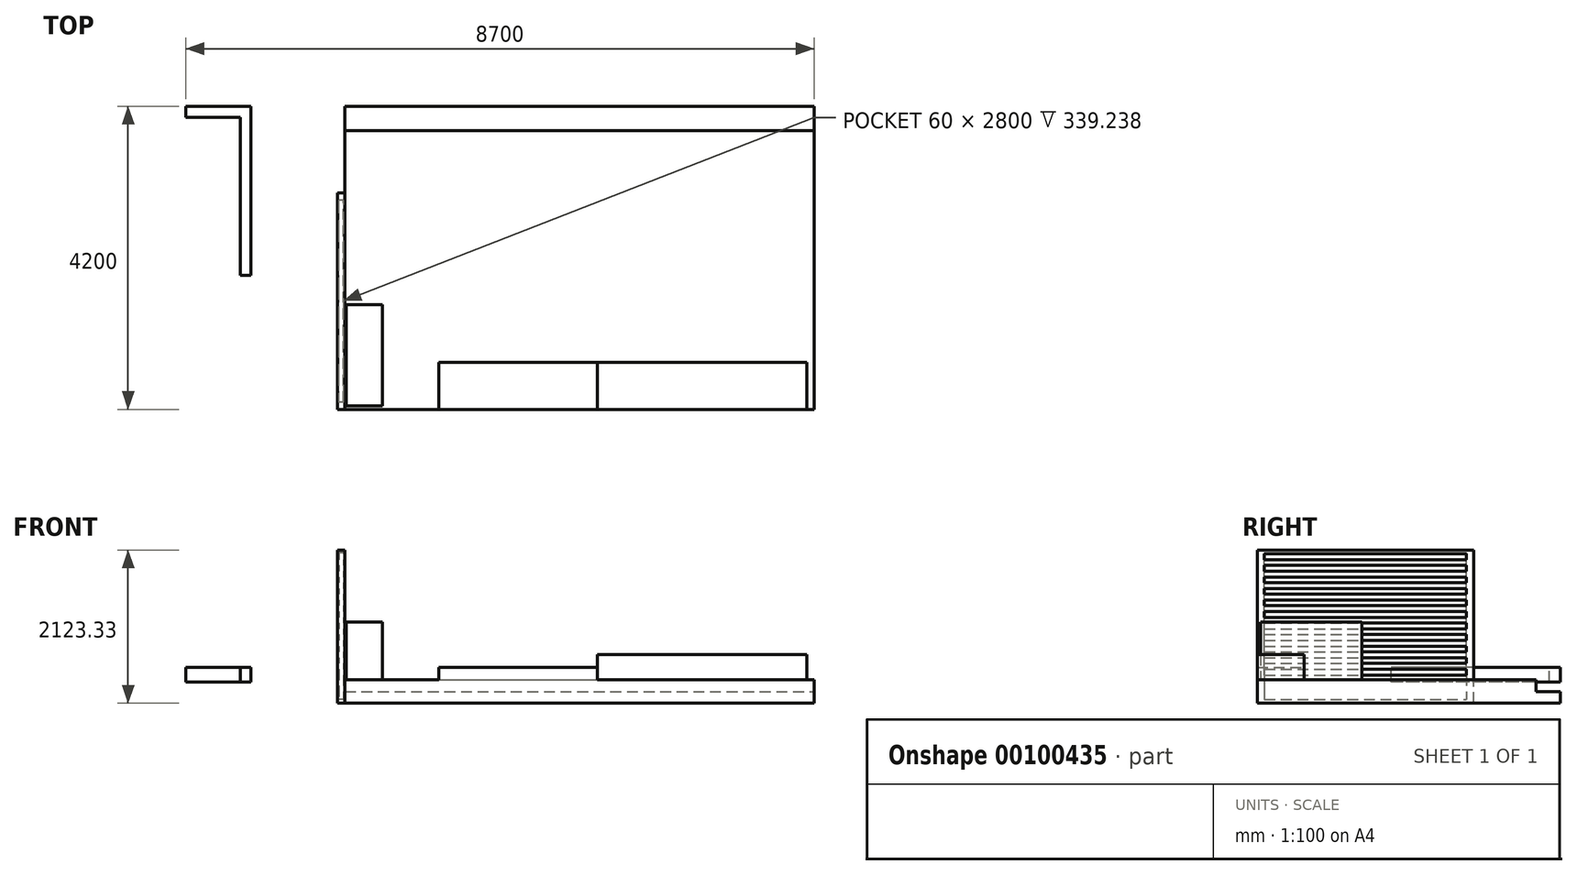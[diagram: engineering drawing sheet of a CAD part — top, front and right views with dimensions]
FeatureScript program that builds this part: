
annotation { "Feature Type Name" : "Feature", "Feature Type Description" : "" }
export const myFeature = defineFeature(function(context is Context, id is Id, definition is map)
    precondition{}
    {
        {
            var Q0;
            Q0=qCreatedBy(makeId("Top.planeOp"),FACE);
            var sketch = newSketch(context, id + "F0", { "sketchPlane" : qUnion([Q0])});
            skLineSegment(sketch, "E0.bottom", {"start": v(0, 0) * mm, "end": v(6600, 0) * mm});
            skLineSegment(sketch, "E0.top", {"start": v(0, -11600) * mm, "end": v(6600, -11600) * mm});
            skLineSegment(sketch, "E0.left", {"start": v(0, 0) * mm, "end": v(0, -11600) * mm});
            skLineSegment(sketch, "E0.right", {"start": v(6600, 0) * mm, "end": v(6600, -11600) * mm});
            skLineSegment(sketch, "E1.bottom", {"start": v(-1200, 1860) * mm, "end": v(0, 1860) * mm});
            skLineSegment(sketch, "E1.top", {"start": v(-1200, -4000) * mm, "end": v(0, -4000) * mm});
            skLineSegment(sketch, "E1.left", {"start": v(-1200, 1860) * mm, "end": v(-1200, -4000) * mm});
            skLineSegment(sketch, "E1.right", {"start": v(0, 1860) * mm, "end": v(0, -4000) * mm});
            skLineSegment(sketch, "E2", {"start": v(-2100, 10600) * mm, "end": v(-2100, 4000) * mm});
            skLineSegment(sketch, "E3", {"start": v(-2100, 4000) * mm, "end": v(-7856.97, 4000) * mm});
            skLineSegment(sketch, "E4", {"start": v(-2100, 10600) * mm, "end": v(-7856.97, 10600) * mm});
            skLineSegment(sketch, "E5", {"start": v(-2100, 4200) * mm, "end": v(-1200, 4200) * mm});
            skLineSegment(sketch, "E6", {"start": v(-1200, 4200) * mm, "end": v(-1200, 1860) * mm});
            skLineSegment(sketch, "E7", {"start": v(300, 0) * mm, "end": v(300, 1860) * mm});
            skLineSegment(sketch, "E8", {"start": v(300, 1860) * mm, "end": v(0, 1860) * mm});
            skLineSegment(sketch, "E9", {"start": v(230, 1860) * mm, "end": v(230, 0) * mm});
            skLineSegment(sketch, "E10.0", {"start": v(-1350, 4050) * mm, "end": v(-1350, 1860) * mm});
            skLineSegment(sketch, "E10.1", {"start": v(-2100, 4050) * mm, "end": v(-1350, 4050) * mm});
            skSolve(sketch);
        }
        {
            var Q0;
            Q0=qCreatedBy(makeId("Top.planeOp"),FACE);
            var sketch = newSketch(context, id + "F1", { "sketchPlane" : qUnion([Q0])});
            skLineSegment(sketch, "E11.0", {"start": v(-2100, 4200) * mm, "end": v(-1200, 4200) * mm});
            skLineSegment(sketch, "E11.1", {"start": v(-2100, 4050) * mm, "end": v(-1350, 4050) * mm});
            skLineSegment(sketch, "E11.2", {"start": v(-1350, 4050) * mm, "end": v(-1350, 1860) * mm});
            skLineSegment(sketch, "E11.3", {"start": v(-1200, 4200) * mm, "end": v(-1200, 1860) * mm});
            skLineSegment(sketch, "E12", {"start": v(-2100, 4200) * mm, "end": v(-2100, 4050) * mm});
            skLineSegment(sketch, "E13", {"start": v(-1200, 1860) * mm, "end": v(-1350, 1860) * mm});
            skSolve(sketch);
        }
        {
            var Q0;
            Q0 = qSketchRegion(id + "F1", true);
            extrude(context, id + "F2", {"entities" : qUnion([Q0]), "oppositeDirection" : true, "depth" : 200 * mm, "offsetDistance" : 25 * mm});
        }
        {
            var Q0;
            Q0=qCreatedBy(makeId("Top.planeOp"),FACE);
            var sketch = newSketch(context, id + "F3", { "sketchPlane" : qUnion([Q0])});
            skLineSegment(sketch, "E14", {"start": v(-1200, 4200) * mm, "end": v(100, 4200) * mm, "construction": true});
            skLineSegment(sketch, "E15", {"start": v(6600, 4200) * mm, "end": v(6600, 0) * mm});
            skLineSegment(sketch, "E16", {"start": v(100, 4200) * mm, "end": v(100, 0) * mm});
            skLineSegment(sketch, "E17", {"start": v(100, 4200) * mm, "end": v(6600, 4200) * mm});
            skLineSegment(sketch, "E18.1", {"start": v(300, 0) * mm, "end": v(6600, 0) * mm});
            skPoint(sketch, "E19.orphan", {"position": v(0, 0) * mm});
            skLineSegment(sketch, "E20", {"start": v(300, 0) * mm, "end": v(100, 0) * mm});
            skSolve(sketch);
        }
        {
            var Q0;
            Q0=qCreatedBy(makeId("Top.planeOp"),FACE);
            var sketch = newSketch(context, id + "F4", { "sketchPlane" : qUnion([Q0])});
            skLineSegment(sketch, "E21.bottom", {"start": v(1450, 0) * mm, "end": v(3550, 0) * mm});
            skLineSegment(sketch, "E21.top", {"start": v(1450, -350) * mm, "end": v(3550, -350) * mm});
            skLineSegment(sketch, "E21.left", {"start": v(1450, 0) * mm, "end": v(1450, -350) * mm});
            skLineSegment(sketch, "E21.right", {"start": v(3550, 0) * mm, "end": v(3550, -350) * mm});
            skLineSegment(sketch, "E22", {"start": v(2350, 0) * mm, "end": v(2350, -350) * mm});
            skLineSegment(sketch, "E23", {"start": v(2350, -175) * mm, "end": v(3550, -175) * mm});
            skSolve(sketch);
        }
        {
            var Q0;
            Q0=qCreatedBy(makeId("Top.planeOp"),FACE);
            cPlane(context, id + "F5", {"entities" : qUnion([Q0]), "cplaneType" : CPlaneType.OFFSET, "offset" : (500 / 3) * mm, "oppositeDirection" : true, "width" : 150 * mm, "height" : 150 * mm});
        }
        {
            var Q0;
            Q0=qCreatedBy(makeId("Top.planeOp"),FACE);
            cPlane(context, id + "F6", {"entities" : qUnion([Q0]), "cplaneType" : CPlaneType.OFFSET, "offset" : (500 / 3 * 2) * mm, "oppositeDirection" : true, "width" : 150 * mm, "height" : 150 * mm});
        }
        {
            var Q0;
            Q0=qCreatedBy(id+"F6.planeOp",FACE);
            cPlane(context, id + "F7", {"entities" : qUnion([Q0]), "cplaneType" : CPlaneType.OFFSET, "offset" : 160 * mm, "oppositeDirection" : true, "width" : 150 * mm, "height" : 150 * mm});
        }
        {
            var Q0;
            Q0=qCreatedBy(makeId("Top.planeOp"),FACE);
            var sketch = newSketch(context, id + "F8", { "sketchPlane" : qUnion([Q0])});
            skLineSegment(sketch, "E24.bottom", {"start": v(1400, 0) * mm, "end": v(3600, 0) * mm});
            skLineSegment(sketch, "E24.top", {"start": v(1400, 650) * mm, "end": v(3600, 650) * mm});
            skLineSegment(sketch, "E24.left", {"start": v(1400, 0) * mm, "end": v(1400, 650) * mm});
            skLineSegment(sketch, "E24.right", {"start": v(3600, 0) * mm, "end": v(3600, 650) * mm});
            skSolve(sketch);
        }
        {
            var Q0;
            Q0 = qSketchRegion(id + "F8", true);
            var Q1;
            Q1=qCreatedBy(id+"F7.planeOp",FACE);
            extrude(context, id + "F9", {"entities" : qUnion([Q0]), "endBound" : BoundingType.UP_TO_SURFACE, "oppositeDirection" : true, "depth" : 25 * mm, "endBoundEntityFace" : qUnion([Q1]), "offsetDistance" : 25 * mm});
        }
        {
            var Q0;
            Q0=qCreatedBy(id+"F5.planeOp",FACE);
            var sketch = newSketch(context, id + "F10", { "sketchPlane" : qUnion([Q0])});
            skLineSegment(sketch, "E25", {"start": v(111.53, 3862.22) * mm, "end": v(6600, 3862.22) * mm});
            skSolve(sketch);
        }
        {
            var Q0;
            Q0=qCreatedBy(id+"F5.planeOp",FACE);
            var sketch = newSketch(context, id + "F11", { "sketchPlane" : qUnion([Q0])});
            skLineSegment(sketch, "E26.0", {"start": v(100, 3862.22) * mm, "end": v(6600, 3862.22) * mm});
            skLineSegment(sketch, "E26.1", {"start": v(6600, 3862.22) * mm, "end": v(6600, 0) * mm});
            skPoint(sketch, "E27.orphan", {"position": v(6600, 4200) * mm});
            skLineSegment(sketch, "E28", {"start": v(100, 3862.22) * mm, "end": v(100, 0) * mm});
            skPoint(sketch, "E29.orphan", {"position": v(111.53, 3862.22) * mm});
            skLineSegment(sketch, "E30", {"start": v(100, 0) * mm, "end": v(1400, 0) * mm});
            skLineSegment(sketch, "E31.0", {"start": v(1400, 0) * mm, "end": v(1400, 650) * mm});
            skLineSegment(sketch, "E31.1", {"start": v(1400, 650) * mm, "end": v(3600, 650) * mm});
            skLineSegment(sketch, "E31.2", {"start": v(3600, 0) * mm, "end": v(3600, 650) * mm});
            skLineSegment(sketch, "E32", {"start": v(3600, 0) * mm, "end": v(6600, 0) * mm});
            skSolve(sketch);
        }
        {
            var Q0;
            Q0 = qSketchRegion(id + "F11", true);
            var Q1;
            Q1=qCreatedBy(id+"F7.planeOp",FACE);
            extrude(context, id + "F12", {"entities" : qUnion([Q0]), "operationType" : NewBodyOperationType.ADD, "endBound" : BoundingType.UP_TO_SURFACE, "oppositeDirection" : true, "depth" : 25 * mm, "endBoundEntityFace" : qUnion([Q1]), "offsetDistance" : 25 * mm});
        }
        {
            var Q0;
            Q0=qCreatedBy(id+"F6.planeOp",FACE);
            var sketch = newSketch(context, id + "F13", { "sketchPlane" : qUnion([Q0])});
            skLineSegment(sketch, "E33.0", {"start": v(100, 4200) * mm, "end": v(6600, 4200) * mm});
            skLineSegment(sketch, "E33.1", {"start": v(6600, 4200) * mm, "end": v(6600, 3862.22) * mm});
            skLineSegment(sketch, "E33.2", {"start": v(100, 3862.22) * mm, "end": v(6600, 3862.22) * mm});
            skLineSegment(sketch, "E33.3", {"start": v(100, 4200) * mm, "end": v(100, 3862.22) * mm});
            skPoint(sketch, "E34.orphan", {"position": v(111.53, 3862.22) * mm});
            skPoint(sketch, "E35.orphan", {"position": v(100, 0) * mm});
            skPoint(sketch, "E36.orphan", {"position": v(6600, 0) * mm});
            skSolve(sketch);
        }
        {
            var Q0;
            Q0 = qSketchRegion(id + "F13", true);
            extrude(context, id + "F14", {"entities" : qUnion([Q0]), "operationType" : NewBodyOperationType.ADD, "oppositeDirection" : true, "depth" : 160 * mm, "offsetDistance" : 25 * mm});
        }
        {
            var Q0;
            Q0=qCreatedBy(makeId("Top.planeOp"),FACE);
            var sketch = newSketch(context, id + "F15", { "sketchPlane" : qUnion([Q0])});
            skLineSegment(sketch, "E37.bottom", {"start": v(5570, 950) * mm, "end": v(3770, 950) * mm});
            skLineSegment(sketch, "E37.top", {"start": v(5570, 1850) * mm, "end": v(3770, 1850) * mm});
            skLineSegment(sketch, "E37.left", {"start": v(5570, 950) * mm, "end": v(5570, 1850) * mm});
            skLineSegment(sketch, "E37.right", {"start": v(3770, 950) * mm, "end": v(3770, 1850) * mm});
            skLineSegment(sketch, "E38.bottom", {"start": v(3600, 0) * mm, "end": v(6500, 0) * mm});
            skLineSegment(sketch, "E38.top", {"start": v(3600, 650) * mm, "end": v(6500, 650) * mm});
            skLineSegment(sketch, "E38.left", {"start": v(3600, 0) * mm, "end": v(3600, 650) * mm});
            skLineSegment(sketch, "E38.right", {"start": v(6500, 0) * mm, "end": v(6500, 650) * mm});
            skLineSegment(sketch, "E39.bottom", {"start": v(6500, 650) * mm, "end": v(5870, 650) * mm});
            skLineSegment(sketch, "E39.top", {"start": v(6500, 2540) * mm, "end": v(5870, 2540) * mm});
            skLineSegment(sketch, "E39.left", {"start": v(6500, 650) * mm, "end": v(6500, 2540) * mm});
            skLineSegment(sketch, "E39.right", {"start": v(5870, 650) * mm, "end": v(5870, 2540) * mm});
            skLineSegment(sketch, "E40.bottom", {"start": v(5570, 950) * mm, "end": v(4670, 950) * mm});
            skLineSegment(sketch, "E40.top", {"start": v(5570, 2750) * mm, "end": v(4670, 2750) * mm});
            skLineSegment(sketch, "E40.left", {"start": v(5570, 950) * mm, "end": v(5570, 2750) * mm});
            skLineSegment(sketch, "E40.right", {"start": v(4670, 950) * mm, "end": v(4670, 2750) * mm});
            skLineSegment(sketch, "E41.bottom", {"start": v(120, 50) * mm, "end": v(620, 50) * mm});
            skLineSegment(sketch, "E41.top", {"start": v(120, 1450) * mm, "end": v(620, 1450) * mm});
            skLineSegment(sketch, "E41.left", {"start": v(120, 50) * mm, "end": v(120, 1450) * mm});
            skLineSegment(sketch, "E41.right", {"start": v(620, 50) * mm, "end": v(620, 1450) * mm});
            skSolve(sketch);
        }
        {
            var Q0;
            Q0=makeQuery(id+"F15.imprint","IMPRINT",FACE,{"disambiguationData":[TD([[makeQuery(id+"F15.imprint","IMPRINT",EDGE,{"derivedFrom":sQuery(id+"F15.wireOp",EDGE,"E38.bottom")}),1.0]])]});
            var Q1;
            Q1=makeQuery(id+"F12.opExtrude","CAP_FACE",FACE,{"disambiguationData":[OSD([sQuery(id+"F11.wireOp",EDGE,"E26.0"),sQuery(id+"F11.wireOp",EDGE,"E26.1"),sQuery(id+"F11.wireOp",EDGE,"E28"),sQuery(id+"F11.wireOp",EDGE,"E30"),sQuery(id+"F11.wireOp",EDGE,"E31.0"),sQuery(id+"F11.wireOp",EDGE,"E31.1"),sQuery(id+"F11.wireOp",EDGE,"E31.2"),sQuery(id+"F11.wireOp",EDGE,"E32")])],"isStart":true});
            extrude(context, id + "F16", {"entities" : qUnion([Q0]), "depth" : (350 - 170) * mm, "offsetDistance" : 25 * mm, "hasSecondDirection" : true, "secondDirectionBound" : BoundingType.UP_TO_SURFACE, "secondDirectionOppositeDirection" : true, "secondDirectionDepth" : 25 * mm, "secondDirectionBoundEntityFace" : qUnion([Q1])});
        }
        {
            var Q0;
            Q0=qCreatedBy(makeId("Top.planeOp"),FACE);
            var sketch = newSketch(context, id + "F17", { "sketchPlane" : qUnion([Q0])});
            skLineSegment(sketch, "E42.bottom", {"start": v(0, 0) * mm, "end": v(100, 0) * mm});
            skLineSegment(sketch, "E42.top", {"start": v(0, 3000) * mm, "end": v(100, 3000) * mm});
            skLineSegment(sketch, "E42.left", {"start": v(0, 0) * mm, "end": v(0, 3000) * mm});
            skLineSegment(sketch, "E42.right", {"start": v(100, 0) * mm, "end": v(100, 3000) * mm});
            skSolve(sketch);
        }
        {
            var Q0;
            Q0 = qSketchRegion(id + "F17", true);
            var Q1;
            Q1=qCreatedBy(id+"F7.planeOp",FACE);
            extrude(context, id + "F18", {"entities" : qUnion([Q0]), "endBound" : BoundingType.UP_TO_SURFACE, "oppositeDirection" : true, "depth" : 25 * mm, "endBoundEntityFace" : qUnion([Q1]), "offsetDistance" : 25 * mm, "hasSecondDirection" : true, "secondDirectionOppositeDirection" : false, "secondDirectionDepth" : (1800 - 170) * mm});
        }
        {
            var Q0;
            Q0=makeQuery(id+"F15.imprint","IMPRINT",FACE,{"disambiguationData":[TD([[makeQuery(id+"F15.imprint","IMPRINT",EDGE,{"derivedFrom":sQuery(id+"F15.wireOp",EDGE,"E41.bottom")}),1.0]])]});
            var Q1;
            Q1=makeQuery(id+"F12.opExtrude","CAP_FACE",FACE,{"disambiguationData":[OSD([sQuery(id+"F11.wireOp",EDGE,"E26.0"),sQuery(id+"F11.wireOp",EDGE,"E26.1"),sQuery(id+"F11.wireOp",EDGE,"E28"),sQuery(id+"F11.wireOp",EDGE,"E30"),sQuery(id+"F11.wireOp",EDGE,"E31.0"),sQuery(id+"F11.wireOp",EDGE,"E31.1"),sQuery(id+"F11.wireOp",EDGE,"E31.2"),sQuery(id+"F11.wireOp",EDGE,"E32")])],"isStart":true});
            extrude(context, id + "F19", {"entities" : qUnion([Q0]), "depth" : (800 - 170) * mm, "offsetDistance" : 25 * mm, "hasSecondDirection" : true, "secondDirectionBound" : BoundingType.UP_TO_SURFACE, "secondDirectionOppositeDirection" : true, "secondDirectionDepth" : 25 * mm, "secondDirectionBoundEntityFace" : qUnion([Q1])});
        }
        {
            var Q0;
            Q0=qCreatedBy(makeId("Front.planeOp"),FACE);
            var sketch = newSketch(context, id + "F20", { "sketchPlane" : qUnion([Q0])});
            skLineSegment(sketch, "E43", {"start": v(0, 0) * mm, "end": v(0, 100) * mm});
            skSolve(sketch);
        }
        {
            var Q0;
            Q0=makeQuery(id+"F18.opExtrude","SWEPT_FACE",FACE,{"disambiguationData":[OSD([sQuery(id+"F17.wireOp",EDGE,"E42.top")])]});
            var sketch = newSketch(context, id + "F21", { "sketchPlane" : qUnion([Q0])});
            skLineSegment(sketch, "E44", {"start": v(-50, 1630) * mm, "end": v(-50, -493.33) * mm, "construction": true});
            skLineSegment(sketch, "E45.bottom", {"start": v(-80, 1590) * mm, "end": v(-20, 1590) * mm});
            skLineSegment(sketch, "E45.top", {"start": v(-80, -443.33) * mm, "end": v(-20, -443.33) * mm});
            skLineSegment(sketch, "E45.left", {"start": v(-80, 1590) * mm, "end": v(-80, -443.33) * mm});
            skLineSegment(sketch, "E45.right", {"start": v(-20, 1590) * mm, "end": v(-20, -443.33) * mm});
            skLineSegment(sketch, "E46.bottom", {"start": v(-80, 1575.9) * mm, "end": v(-100, 1575.9) * mm});
            skLineSegment(sketch, "E46.top", {"start": v(-80, 1495.9) * mm, "end": v(-100, 1495.9) * mm});
            skLineSegment(sketch, "E46.left", {"start": v(-80, 1575.9) * mm, "end": v(-80, 1495.9) * mm});
            skLineSegment(sketch, "E46.right", {"start": v(-100, 1575.9) * mm, "end": v(-100, 1495.9) * mm});
            skLineSegment(sketch, "E47.bottom", {"start": v(-20, 1495.9) * mm, "end": v(0, 1495.9) * mm});
            skLineSegment(sketch, "E47.top", {"start": v(-20, 1415.9) * mm, "end": v(0, 1415.9) * mm});
            skLineSegment(sketch, "E47.left", {"start": v(-20, 1495.9) * mm, "end": v(-20, 1415.9) * mm});
            skLineSegment(sketch, "E47.right", {"start": v(0, 1495.9) * mm, "end": v(0, 1415.9) * mm});
            skLineSegment(sketch, "E48.bottom", {"start": v(-80, 1415.9) * mm, "end": v(-100, 1415.9) * mm});
            skLineSegment(sketch, "E48.top", {"start": v(-80, 1335.9) * mm, "end": v(-100, 1335.9) * mm});
            skLineSegment(sketch, "E48.left", {"start": v(-80, 1415.9) * mm, "end": v(-80, 1335.9) * mm});
            skLineSegment(sketch, "E48.right", {"start": v(-100, 1415.9) * mm, "end": v(-100, 1335.9) * mm});
            skLineSegment(sketch, "E49.bottom", {"start": v(-20, 1335.9) * mm, "end": v(0, 1335.9) * mm});
            skLineSegment(sketch, "E49.top", {"start": v(-20, 1255.9) * mm, "end": v(0, 1255.9) * mm});
            skLineSegment(sketch, "E49.left", {"start": v(-20, 1335.9) * mm, "end": v(-20, 1255.9) * mm});
            skLineSegment(sketch, "E49.right", {"start": v(0, 1335.9) * mm, "end": v(0, 1255.9) * mm});
            skLineSegment(sketch, "E50.bottom", {"start": v(-80, 1255.9) * mm, "end": v(-100, 1255.9) * mm});
            skLineSegment(sketch, "E50.top", {"start": v(-80, 1175.9) * mm, "end": v(-100, 1175.9) * mm});
            skLineSegment(sketch, "E50.left", {"start": v(-80, 1255.9) * mm, "end": v(-80, 1175.9) * mm});
            skLineSegment(sketch, "E50.right", {"start": v(-100, 1255.9) * mm, "end": v(-100, 1175.9) * mm});
            skLineSegment(sketch, "E51.bottom", {"start": v(-20, 1175.9) * mm, "end": v(0, 1175.9) * mm});
            skLineSegment(sketch, "E51.top", {"start": v(-20, 1095.9) * mm, "end": v(0, 1095.9) * mm});
            skLineSegment(sketch, "E51.left", {"start": v(-20, 1175.9) * mm, "end": v(-20, 1095.9) * mm});
            skLineSegment(sketch, "E51.right", {"start": v(0, 1175.9) * mm, "end": v(0, 1095.9) * mm});
            skLineSegment(sketch, "E52.bottom", {"start": v(-80, 1095.9) * mm, "end": v(-100, 1095.9) * mm});
            skLineSegment(sketch, "E52.top", {"start": v(-80, 1015.9) * mm, "end": v(-100, 1015.9) * mm});
            skLineSegment(sketch, "E52.left", {"start": v(-80, 1095.9) * mm, "end": v(-80, 1015.9) * mm});
            skLineSegment(sketch, "E52.right", {"start": v(-100, 1095.9) * mm, "end": v(-100, 1015.9) * mm});
            skLineSegment(sketch, "E53.bottom", {"start": v(-20, 1015.9) * mm, "end": v(0, 1015.9) * mm});
            skLineSegment(sketch, "E53.top", {"start": v(-20, 935.9) * mm, "end": v(0, 935.9) * mm});
            skLineSegment(sketch, "E53.left", {"start": v(-20, 1015.9) * mm, "end": v(-20, 935.9) * mm});
            skLineSegment(sketch, "E53.right", {"start": v(0, 1015.9) * mm, "end": v(0, 935.9) * mm});
            skLineSegment(sketch, "E54.bottom", {"start": v(-80, 935.9) * mm, "end": v(-100, 935.9) * mm});
            skLineSegment(sketch, "E54.top", {"start": v(-80, 855.9) * mm, "end": v(-100, 855.9) * mm});
            skLineSegment(sketch, "E54.left", {"start": v(-80, 935.9) * mm, "end": v(-80, 855.9) * mm});
            skLineSegment(sketch, "E54.right", {"start": v(-100, 935.9) * mm, "end": v(-100, 855.9) * mm});
            skLineSegment(sketch, "E55.bottom", {"start": v(-20, 855.9) * mm, "end": v(0, 855.9) * mm});
            skLineSegment(sketch, "E55.top", {"start": v(-20, 775.9) * mm, "end": v(0, 775.9) * mm});
            skLineSegment(sketch, "E55.left", {"start": v(-20, 855.9) * mm, "end": v(-20, 775.9) * mm});
            skLineSegment(sketch, "E55.right", {"start": v(0, 855.9) * mm, "end": v(0, 775.9) * mm});
            skLineSegment(sketch, "E56.bottom", {"start": v(-80, 775.9) * mm, "end": v(-100, 775.9) * mm});
            skLineSegment(sketch, "E56.top", {"start": v(-80, 695.9) * mm, "end": v(-100, 695.9) * mm});
            skLineSegment(sketch, "E56.left", {"start": v(-80, 775.9) * mm, "end": v(-80, 695.9) * mm});
            skLineSegment(sketch, "E56.right", {"start": v(-100, 775.9) * mm, "end": v(-100, 695.9) * mm});
            skLineSegment(sketch, "E57.bottom", {"start": v(-20, 695.9) * mm, "end": v(0, 695.9) * mm});
            skLineSegment(sketch, "E57.top", {"start": v(-20, 615.9) * mm, "end": v(0, 615.9) * mm});
            skLineSegment(sketch, "E57.left", {"start": v(-20, 695.9) * mm, "end": v(-20, 615.9) * mm});
            skLineSegment(sketch, "E57.right", {"start": v(0, 695.9) * mm, "end": v(0, 615.9) * mm});
            skLineSegment(sketch, "E58.bottom", {"start": v(-80, 615.9) * mm, "end": v(-100, 615.9) * mm});
            skLineSegment(sketch, "E58.top", {"start": v(-80, 535.9) * mm, "end": v(-100, 535.9) * mm});
            skLineSegment(sketch, "E58.left", {"start": v(-80, 615.9) * mm, "end": v(-80, 535.9) * mm});
            skLineSegment(sketch, "E58.right", {"start": v(-100, 615.9) * mm, "end": v(-100, 535.9) * mm});
            skLineSegment(sketch, "E59.bottom", {"start": v(-20, 535.9) * mm, "end": v(0, 535.9) * mm});
            skLineSegment(sketch, "E59.top", {"start": v(-20, 455.9) * mm, "end": v(0, 455.9) * mm});
            skLineSegment(sketch, "E59.left", {"start": v(-20, 535.9) * mm, "end": v(-20, 455.9) * mm});
            skLineSegment(sketch, "E59.right", {"start": v(0, 535.9) * mm, "end": v(0, 455.9) * mm});
            skLineSegment(sketch, "E60.bottom", {"start": v(-80, 455.9) * mm, "end": v(-100, 455.9) * mm});
            skLineSegment(sketch, "E60.top", {"start": v(-80, 375.9) * mm, "end": v(-100, 375.9) * mm});
            skLineSegment(sketch, "E60.left", {"start": v(-80, 455.9) * mm, "end": v(-80, 375.9) * mm});
            skLineSegment(sketch, "E60.right", {"start": v(-100, 455.9) * mm, "end": v(-100, 375.9) * mm});
            skLineSegment(sketch, "E61.bottom", {"start": v(-20, 375.9) * mm, "end": v(0, 375.9) * mm});
            skLineSegment(sketch, "E61.top", {"start": v(-20, 295.9) * mm, "end": v(0, 295.9) * mm});
            skLineSegment(sketch, "E61.left", {"start": v(-20, 375.9) * mm, "end": v(-20, 295.9) * mm});
            skLineSegment(sketch, "E61.right", {"start": v(0, 375.9) * mm, "end": v(0, 295.9) * mm});
            skLineSegment(sketch, "E62.bottom", {"start": v(-80, 295.9) * mm, "end": v(-100, 295.9) * mm});
            skLineSegment(sketch, "E62.top", {"start": v(-80, 215.9) * mm, "end": v(-100, 215.9) * mm});
            skLineSegment(sketch, "E62.left", {"start": v(-80, 295.9) * mm, "end": v(-80, 215.9) * mm});
            skLineSegment(sketch, "E62.right", {"start": v(-100, 295.9) * mm, "end": v(-100, 215.9) * mm});
            skLineSegment(sketch, "E63.bottom", {"start": v(-20, 215.9) * mm, "end": v(0, 215.9) * mm});
            skLineSegment(sketch, "E63.top", {"start": v(-20, 135.9) * mm, "end": v(0, 135.9) * mm});
            skLineSegment(sketch, "E63.left", {"start": v(-20, 215.9) * mm, "end": v(-20, 135.9) * mm});
            skLineSegment(sketch, "E63.right", {"start": v(0, 215.9) * mm, "end": v(0, 135.9) * mm});
            skLineSegment(sketch, "E64.bottom", {"start": v(-80, 135.9) * mm, "end": v(-100, 135.9) * mm});
            skLineSegment(sketch, "E64.top", {"start": v(-80, 55.9) * mm, "end": v(-100, 55.9) * mm});
            skLineSegment(sketch, "E64.left", {"start": v(-80, 135.9) * mm, "end": v(-80, 55.9) * mm});
            skLineSegment(sketch, "E64.right", {"start": v(-100, 135.9) * mm, "end": v(-100, 55.9) * mm});
            skLineSegment(sketch, "E65.bottom", {"start": v(-20, 55.9) * mm, "end": v(0, 55.9) * mm});
            skLineSegment(sketch, "E65.top", {"start": v(-20, -24.1) * mm, "end": v(0, -24.1) * mm});
            skLineSegment(sketch, "E65.left", {"start": v(-20, 55.9) * mm, "end": v(-20, -24.1) * mm});
            skLineSegment(sketch, "E65.right", {"start": v(0, 55.9) * mm, "end": v(0, -24.1) * mm});
            skLineSegment(sketch, "E66.bottom", {"start": v(-80, -24.1) * mm, "end": v(-100, -24.1) * mm});
            skLineSegment(sketch, "E66.top", {"start": v(-80, -104.1) * mm, "end": v(-100, -104.1) * mm});
            skLineSegment(sketch, "E66.left", {"start": v(-80, -24.1) * mm, "end": v(-80, -104.1) * mm});
            skLineSegment(sketch, "E66.right", {"start": v(-100, -24.1) * mm, "end": v(-100, -104.1) * mm});
            skSolve(sketch);
        }
        {
            var Q0;
            Q0 = qSketchRegion(id + "F21", true);
            var Q1;
            Q1=makeQuery(id+"F18.opExtrude","SWEPT_FACE",FACE,{"disambiguationData":[OSD([sQuery(id+"F17.wireOp",EDGE,"E42.bottom")])]});
            extrude(context, id + "F22", {"entities" : qUnion([Q0]), "operationType" : NewBodyOperationType.REMOVE, "oppositeDirection" : true, "depth" : (3000 - 100) * mm, "endBoundEntityFace" : qUnion([Q1]), "offsetDistance" : 25 * mm, "hasSecondDirection" : true, "secondDirectionOppositeDirection" : true, "secondDirectionDepth" : 100 * mm});
        }
    });
